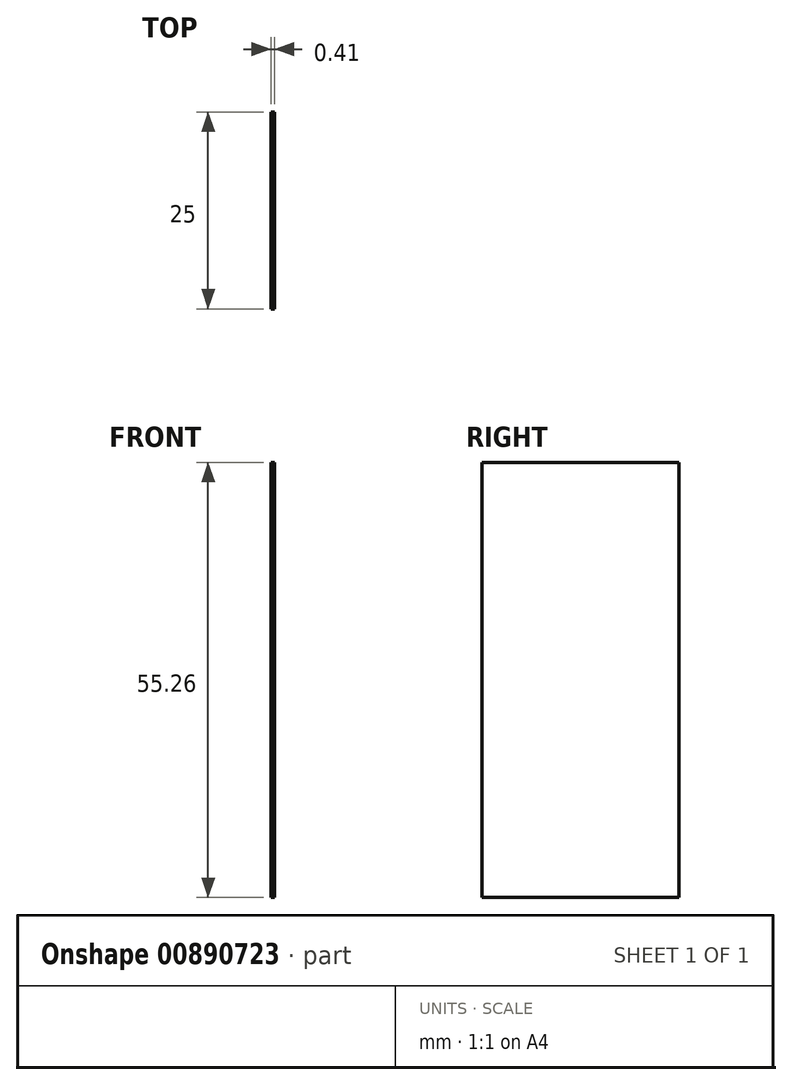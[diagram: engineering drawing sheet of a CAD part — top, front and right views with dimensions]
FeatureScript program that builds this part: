
annotation { "Feature Type Name" : "Feature", "Feature Type Description" : "" }
export const myFeature = defineFeature(function(context is Context, id is Id, definition is map)
    precondition{}
    {
        {
            var Q0;
            Q0=qCreatedBy(makeId("Front.planeOp"),FACE);
            var sketch = newSketch(context, id + "F0", { "sketchPlane" : qUnion([Q0])});
            skLineSegment(sketch, "E0", {"start": v(-49.93, 26.9) * mm, "end": v(31.23, 26.9) * mm});
            skLineSegment(sketch, "E1", {"start": v(-46.77, 48.5) * mm, "end": v(30.94, 48.5) * mm});
            skLineSegment(sketch, "E2", {"start": v(53.39, 43.9) * mm, "end": v(53.39, -11.37) * mm});
            skLineSegment(sketch, "E3", {"start": v(53.39, -11.37) * mm, "end": v(52.98, -11.37) * mm});
            skLineSegment(sketch, "E4", {"start": v(52.98, -11.37) * mm, "end": v(52.98, 43.9) * mm});
            skLineSegment(sketch, "E5", {"start": v(52.98, 43.9) * mm, "end": v(53.39, 43.9) * mm});
            skLineSegment(sketch, "E6.bottom", {"start": v(-25, 25.62) * mm, "end": v(25, 25.62) * mm});
            skLineSegment(sketch, "E6.top", {"start": v(-25, -24.38) * mm, "end": v(25, -24.38) * mm});
            skLineSegment(sketch, "E6.left", {"start": v(-25, 25.62) * mm, "end": v(-25, -24.38) * mm});
            skLineSegment(sketch, "E6.right", {"start": v(25, 25.62) * mm, "end": v(25, -24.38) * mm});
            skPoint(sketch, "E6.middle", {"position": v(0, 0.62) * mm});
            skSolve(sketch);
        }
        {
            var Q0;
            Q0=makeQuery(id+"F0.imprint","IMPRINT",FACE,{"disambiguationData":[TD([[makeQuery(id+"F0.imprint","IMPRINT",EDGE,{"derivedFrom":sQuery(id+"F0.wireOp",EDGE,"E2")}),-1.0]])]});
            extrude(context, id + "F1", {"entities" : qUnion([Q0]), "depth" : 25 * mm, "offsetDistance" : 25 * mm});
        }
    });
